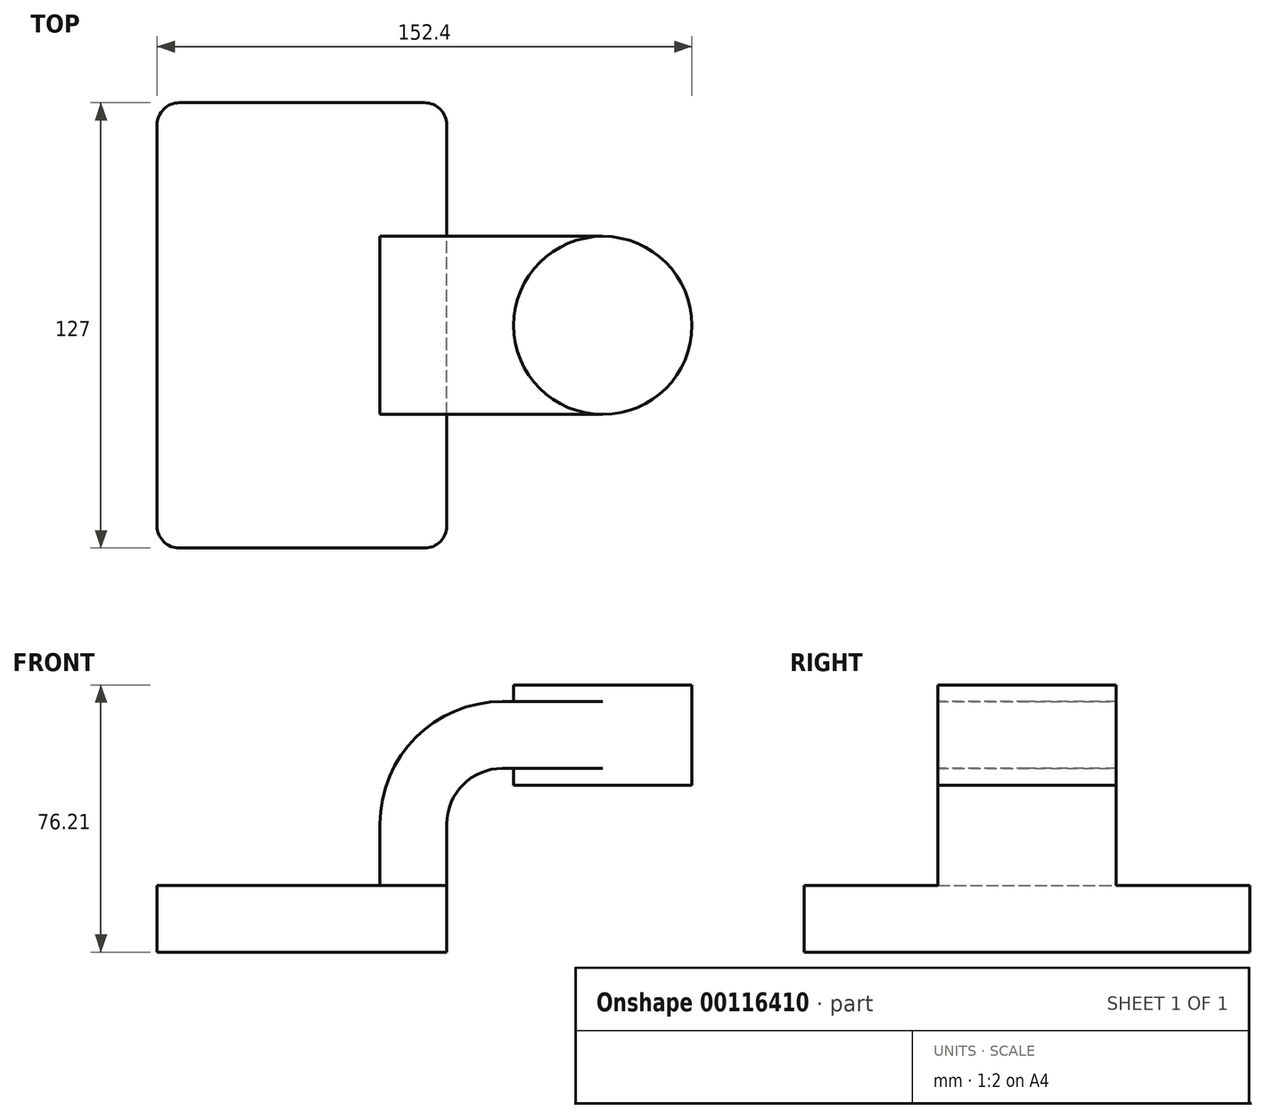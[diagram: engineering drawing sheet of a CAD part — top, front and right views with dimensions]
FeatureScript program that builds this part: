
annotation { "Feature Type Name" : "Feature", "Feature Type Description" : "" }
export const myFeature = defineFeature(function(context is Context, id is Id, definition is map)
    precondition{}
    {
        {
            var Q0;
            Q0=qCreatedBy(makeId("Front.planeOp"),FACE);
            var sketch = newSketch(context, id + "F0", { "sketchPlane" : qUnion([Q0])});
            skLineSegment(sketch, "E0.bottom", {"start": v(-41.28, 9.52) * mm, "end": v(41.28, 9.52) * mm});
            skLineSegment(sketch, "E0.top", {"start": v(-41.28, -9.53) * mm, "end": v(41.27, -9.53) * mm});
            skLineSegment(sketch, "E0.left", {"start": v(-41.28, 9.52) * mm, "end": v(-41.28, -9.53) * mm});
            skLineSegment(sketch, "E0.right", {"start": v(41.27, 9.52) * mm, "end": v(41.27, -9.53) * mm});
            skPoint(sketch, "E0.middle", {"position": v(0, 0) * mm});
            skLineSegment(sketch, "E1.bottom", {"start": v(111.12, 38.1) * mm, "end": v(60.32, 38.1) * mm});
            skLineSegment(sketch, "E1.top", {"start": v(111.12, 66.67) * mm, "end": v(60.32, 66.67) * mm});
            skLineSegment(sketch, "E1.left", {"start": v(111.12, 38.1) * mm, "end": v(111.12, 66.67) * mm});
            skLineSegment(sketch, "E1.right", {"start": v(60.32, 38.1) * mm, "end": v(60.32, 66.67) * mm});
            skPoint(sketch, "E1.middle", {"position": v(85.72, 52.39) * mm});
            skLineSegment(sketch, "E2", {"start": v(41.28, 9.52) * mm, "end": v(41.28, 27) * mm});
            skPoint(sketch, "E3.endSnap0", {"position": v(60.32, 52.39) * mm});
            skArc(sketch, "E4", {"start": v(41.27, 27) * mm, "mid": v(45.92, 38.23) * mm, "end": v(57.15, 42.88) * mm});
            skLineSegment(sketch, "E5", {"start": v(57.15, 42.88) * mm, "end": v(85.72, 42.88) * mm});
            skLineSegment(sketch, "E6.0", {"start": v(57.15, 61.93) * mm, "end": v(85.72, 61.93) * mm});
            skArc(sketch, "E6.1", {"start": v(22.22, 27) * mm, "mid": v(32.45, 51.7) * mm, "end": v(57.15, 61.93) * mm});
            skLineSegment(sketch, "E6.2", {"start": v(22.22, 9.52) * mm, "end": v(22.22, 27) * mm});
            skLineSegment(sketch, "E7", {"start": v(85.72, 38.1) * mm, "end": v(85.72, 66.67) * mm});
            skFitSpline(sketch, "E8", {"points": [v(-41.28, 9.52) * mm, v(57.15, 61.93) * mm], "startDerivative": vector(0.98, 59.65) * mm, "endDerivative": vector(171.45, -1) * mm});
            skSolve(sketch);
        }
        {
            var Q0;
            Q0=makeQuery(id+"F0.imprint","IMPRINT",FACE,{"disambiguationData":[TD([[makeQuery(id+"F0.imprint","IMPRINT",EDGE,{"derivedFrom":sQuery(id+"F0.wireOp",EDGE,"E0.top")}),1.0]])]});
            extrude(context, id + "F1", {"entities" : qUnion([Q0]), "endBound" : BoundingType.SYMMETRIC, "depth" : 127 * mm});
        }
        {
            var Q0;
            {var subQ1=sQuery(id+"F0.wireOp",EDGE,"E2");Q0=makeQuery(id+"F0.imprint","IMPRINT",FACE,{"disambiguationData":[TD([[makeQuery(id+"F0.imprint","IMPRINT",EDGE,{"derivedFrom":subQ1}),1.0]])]});}
            var Q1;
            {var subQ0=sQuery(id+"F0.wireOp",EDGE,"E5");var subQ1=sQuery(id+"F0.wireOp",EDGE,"E1.right");var subQ2=makeQuery(id+"F0.imprint","INTERSECT",VERTEX,{"derivedFrom":[subQ1,subQ0]});Q1=makeQuery(id+"F0.imprint","IMPRINT",FACE,{"disambiguationData":[TD([[makeQuery(id+"F0.imprint","IMPRINT",EDGE,{"disambiguationData":[TD([[subQ2,-1.0]])],"derivedFrom":subQ1}),-1.0]])]});}
            extrude(context, id + "F2", {"entities" : qUnion([Q0, Q1]), "operationType" : NewBodyOperationType.ADD, "endBound" : BoundingType.SYMMETRIC, "depth" : 50.8 * mm});
        }
        {
            var Q0;
            Q0=makeQuery(id+"F0.imprint","IMPRINT",FACE,{"disambiguationData":[TD([[makeQuery(id+"F0.imprint","IMPRINT",EDGE,{"derivedFrom":sQuery(id+"F0.wireOp",EDGE,"E6.1")}),1.0]])]});
            extrude(context, id + "F3", {"entities" : qUnion([Q0]), "operationType" : NewBodyOperationType.ADD, "endBound" : BoundingType.SYMMETRIC, "depth" : 15.88 * mm});
        }
        {
            var Q0;
            {var subQ0=sQuery(id+"F0.wireOp",EDGE,"E1.left");Q0=makeQuery(id+"F0.imprint","IMPRINT",FACE,{"disambiguationData":[TD([[makeQuery(id+"F0.imprint","IMPRINT",EDGE,{"derivedFrom":subQ0}),1.0]])]});}
            var Q1;
            Q1=sQuery(id+"F0.wireOp",EDGE,"E7");
            revolve(context, id + "F4", {"operationType" : NewBodyOperationType.ADD, "entities" : qUnion([Q0]), "axis" : qUnion([Q1]), "revolveType" : RevolveType.FULL});
        }
        {
            var Q0;
            Q0=makeQuery(id+"F1.opExtrude","CAP_EDGE",EDGE,{"disambiguationData":[OSD([sQuery(id+"F0.wireOp",EDGE,"E0.right")])],"isStart":false});
            var Q1;
            Q1=makeQuery(id+"F1.opExtrude","CAP_EDGE",EDGE,{"disambiguationData":[OSD([sQuery(id+"F0.wireOp",EDGE,"E0.left")])],"isStart":false});
            var Q2;
            Q2=makeQuery(id+"F1.opExtrude","CAP_EDGE",EDGE,{"disambiguationData":[OSD([sQuery(id+"F0.wireOp",EDGE,"E0.right")])],"isStart":true});
            var Q3;
            Q3=makeQuery(id+"F1.opExtrude","CAP_EDGE",EDGE,{"disambiguationData":[OSD([sQuery(id+"F0.wireOp",EDGE,"E0.left")])],"isStart":true});
            fillet(context, id + "F5", {"entities" : qUnion([Q0, Q1, Q2, Q3]), "radius" : 6.35 * mm, "tangentPropagation" : true, "allowEdgeOverflow" : false});
        }
    });
